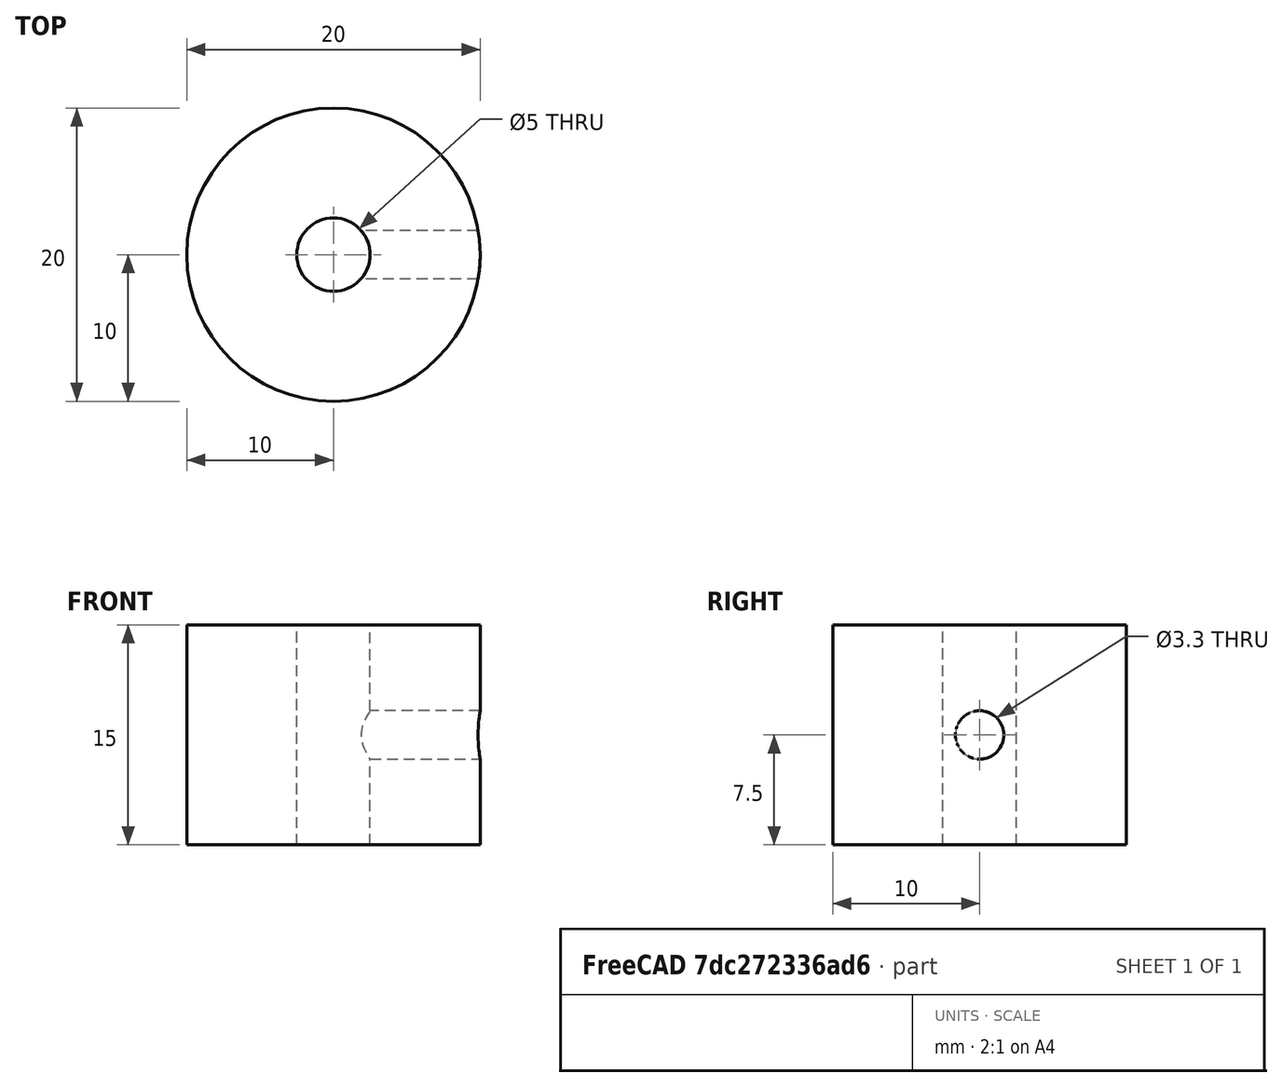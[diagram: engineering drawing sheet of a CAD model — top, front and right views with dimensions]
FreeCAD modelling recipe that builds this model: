
FCSTD DOCUMENT  (FreeCAD 0.21R33771 (Git))
Label: SFT-Mk5-Rotor Bush
License: Public Domain
LicenseURL: https://en.wikipedia.org/wiki/Public_domain
objects: PartDesign::CoordinateSystem×1, Part::FeaturePython×1, Part::Cylinder×1, Part::Cut×1, PartDesign::Line×1, App::Part×1
note: 5 computed .brp shape members not serialized (recipe doc carries the construction recipe); baked Part::Feature solids carry a one-line shape summary decoded from their .brp

FEATURE [PartDesign::CoordinateSystem] LCS_Origin
  AttacherType = Attacher::AttachEngine3D
  MapMode = 2
  Support = -> [X_Axis]
FEATURE [Part::FeaturePython] Tube  label="Bush"  # WARN: FeaturePython — macro-defined, semantics opaque (R4)
  AttacherType = Attacher::AttachEngine3D
  Height = 15
  InnerRadius = 2.5
  OuterRadius = 10
FEATURE [Part::Cylinder] Cylinder  label="Grubscrew Hole"
  Angle = 360
  AttacherType = Attacher::AttachEngine3D
  FirstAngle = 0
  Height = 10
  Placement = pos=(1,0,7.5) rot=(0,1,0;1.5708rad)
  Radius = 1.65
  SecondAngle = 0
FEATURE [Part::Cut] Cut
  Base = -> Tube
  Tool = -> Cylinder
FEATURE [PartDesign::Line] HoleAxis_1  label="Grubscrew AP"
  AttacherType = Attacher::AttachEngineLine
  Length = 7.04534
  MapMode = 19
  Placement = pos=(9.73495,-9e-16,7.54372) rot=(-0.762498,0,-0.646991;3.14159rad)
  ResizeMode = 1
  Support = -> [Cut]
FEATURE [App::Part] Rotor_Bush  label="Rotor Bush"
  Group = -> [LCS_Origin,Tube,Cylinder,Cut,HoleAxis_1]
  Origin = -> Origin
